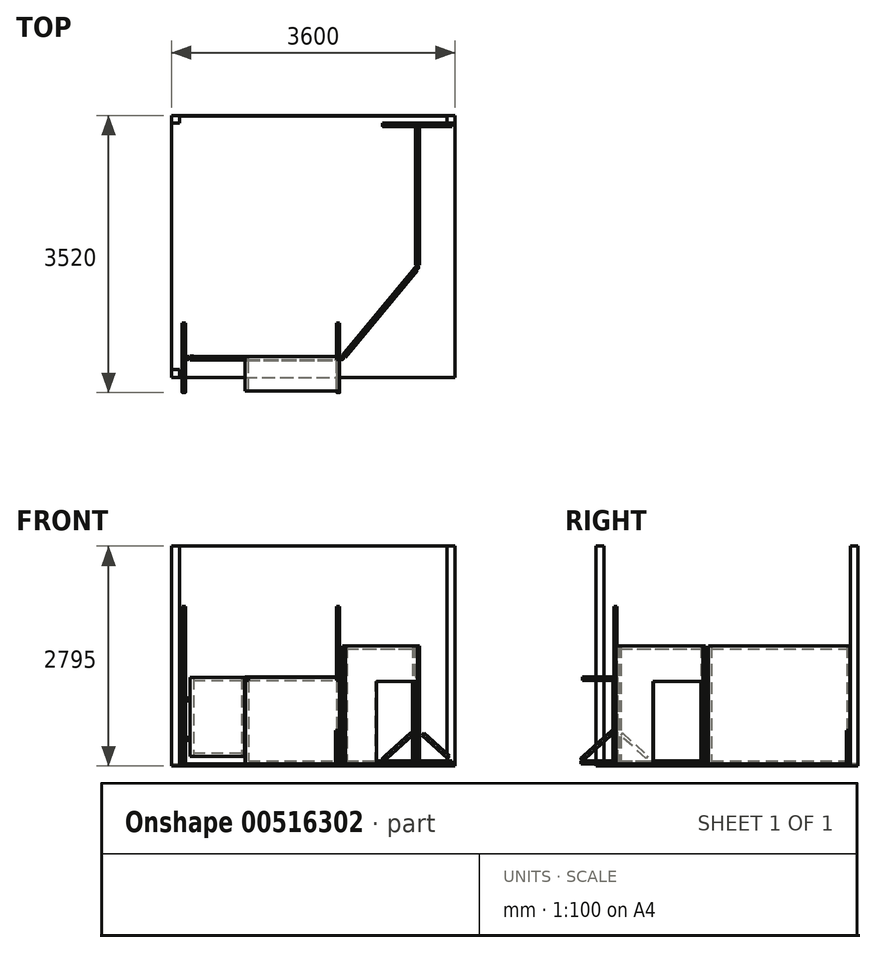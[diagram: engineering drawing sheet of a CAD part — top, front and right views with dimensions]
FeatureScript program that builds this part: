
annotation { "Feature Type Name" : "Feature", "Feature Type Description" : "" }
export const myFeature = defineFeature(function(context is Context, id is Id, definition is map)
    precondition{}
    {
        {
            var Q0;
            Q0=qCreatedBy(makeId("Top.planeOp"),FACE);
            var sketch = newSketch(context, id + "F0", { "sketchPlane" : qUnion([Q0])});
            skLineSegment(sketch, "E0.bottom", {"start": v(-1797.14, 1651.1) * mm, "end": v(1802.86, 1651.1) * mm});
            skLineSegment(sketch, "E0.top", {"start": v(-1797.14, -1678.9) * mm, "end": v(1802.86, -1678.9) * mm});
            skLineSegment(sketch, "E0.left", {"start": v(-1797.14, 1651.1) * mm, "end": v(-1797.14, -1678.9) * mm});
            skLineSegment(sketch, "E0.right", {"start": v(1802.86, 1651.1) * mm, "end": v(1802.86, -1678.9) * mm});
            skSolve(sketch);
        }
        {
            var Q0;
            Q0=makeQuery(id+"F0.imprint","IMPRINT",FACE,{"disambiguationData":[TD([[makeQuery(id+"F0.imprint","IMPRINT",EDGE,{"derivedFrom":sQuery(id+"F0.wireOp",EDGE,"E0.bottom")}),-1.0]])]});
            extrude(context, id + "F1", {"entities" : qUnion([Q0]), "depth" : 25 * mm, "offsetDistance" : 25 * mm});
        }
        {
            var Q0;
            Q0=makeQuery(id+"F1.opExtrude","CAP_FACE",FACE,{"disambiguationData":[OSD([sQuery(id+"F0.wireOp",EDGE,"E0.bottom"),sQuery(id+"F0.wireOp",EDGE,"E0.top"),sQuery(id+"F0.wireOp",EDGE,"E0.left"),sQuery(id+"F0.wireOp",EDGE,"E0.right")])],"isStart":false});
            var sketch = newSketch(context, id + "F2", { "sketchPlane" : qUnion([Q0])});
            skLineSegment(sketch, "E1.bottom", {"start": v(-1797.14, 1651.1) * mm, "end": v(-1697.14, 1651.1) * mm});
            skLineSegment(sketch, "E1.top", {"start": v(-1797.14, 1551.1) * mm, "end": v(-1697.14, 1551.1) * mm});
            skLineSegment(sketch, "E1.left", {"start": v(-1797.14, 1651.1) * mm, "end": v(-1797.14, 1551.1) * mm});
            skLineSegment(sketch, "E1.right", {"start": v(-1697.14, 1651.1) * mm, "end": v(-1697.14, 1551.1) * mm});
            skLineSegment(sketch, "E2.bottom", {"start": v(-1797.14, -1678.9) * mm, "end": v(-1697.14, -1678.9) * mm});
            skLineSegment(sketch, "E2.top", {"start": v(-1797.14, -1578.9) * mm, "end": v(-1697.14, -1578.9) * mm});
            skLineSegment(sketch, "E2.left", {"start": v(-1797.14, -1678.9) * mm, "end": v(-1797.14, -1578.9) * mm});
            skLineSegment(sketch, "E2.right", {"start": v(-1697.14, -1678.9) * mm, "end": v(-1697.14, -1578.9) * mm});
            skLineSegment(sketch, "E3.bottom", {"start": v(1802.86, 1651.1) * mm, "end": v(1702.86, 1651.1) * mm});
            skLineSegment(sketch, "E3.top", {"start": v(1802.86, 1551.1) * mm, "end": v(1702.86, 1551.1) * mm});
            skLineSegment(sketch, "E3.left", {"start": v(1802.86, 1651.1) * mm, "end": v(1802.86, 1551.1) * mm});
            skLineSegment(sketch, "E3.right", {"start": v(1702.86, 1651.1) * mm, "end": v(1702.86, 1551.1) * mm});
            skLineSegment(sketch, "E4.bottom", {"start": v(-1697.14, 1651.1) * mm, "end": v(1702.86, 1651.1) * mm});
            skLineSegment(sketch, "E4.top", {"start": v(-1697.14, 1641.1) * mm, "end": v(1702.86, 1641.1) * mm});
            skLineSegment(sketch, "E4.left", {"start": v(-1697.14, 1651.1) * mm, "end": v(-1697.14, 1641.1) * mm});
            skLineSegment(sketch, "E4.right", {"start": v(1702.86, 1651.1) * mm, "end": v(1702.86, 1641.1) * mm});
            skLineSegment(sketch, "E5.bottom", {"start": v(-1797.14, 1551.1) * mm, "end": v(-1787.14, 1551.1) * mm});
            skLineSegment(sketch, "E5.top", {"start": v(-1797.14, -1578.9) * mm, "end": v(-1787.14, -1578.9) * mm});
            skLineSegment(sketch, "E5.left", {"start": v(-1797.14, 1551.1) * mm, "end": v(-1797.14, -1578.9) * mm});
            skLineSegment(sketch, "E5.right", {"start": v(-1787.14, 1551.1) * mm, "end": v(-1787.14, -1578.9) * mm});
            skSolve(sketch);
        }
        {
            var Q0;
            Q0=makeQuery(id+"F2.imprint","IMPRINT",FACE,{"disambiguationData":[TD([[makeQuery(id+"F2.imprint","IMPRINT",EDGE,{"derivedFrom":sQuery(id+"F2.wireOp",EDGE,"E1.bottom")}),-1.0]])]});
            var Q1;
            Q1=makeQuery(id+"F2.imprint","IMPRINT",FACE,{"disambiguationData":[TD([[makeQuery(id+"F2.imprint","IMPRINT",EDGE,{"derivedFrom":sQuery(id+"F2.wireOp",EDGE,"E2.bottom")}),1.0]])]});
            var Q2;
            Q2=makeQuery(id+"F2.imprint","IMPRINT",FACE,{"disambiguationData":[TD([[makeQuery(id+"F2.imprint","IMPRINT",EDGE,{"derivedFrom":sQuery(id+"F2.wireOp",EDGE,"rSnRhUeP-VmXx-mMHw-5nAW-2HBpdxi9ySfm.bottom")}),1.0]])]});
            var Q3;
            Q3=makeQuery(id+"F2.imprint","IMPRINT",FACE,{"disambiguationData":[TD([[makeQuery(id+"F2.imprint","IMPRINT",EDGE,{"derivedFrom":sQuery(id+"F2.wireOp",EDGE,"E3.bottom")}),-1.0]])]});
            var Q4;
            Q4=makeQuery(id+"F2.imprint","IMPRINT",FACE,{"disambiguationData":[TD([[makeQuery(id+"F2.imprint","IMPRINT",EDGE,{"derivedFrom":sQuery(id+"F2.wireOp",EDGE,"E5.bottom")}),-1.0]])]});
            var Q5;
            Q5=makeQuery(id+"F2.imprint","IMPRINT",FACE,{"disambiguationData":[TD([[makeQuery(id+"F2.imprint","IMPRINT",EDGE,{"derivedFrom":sQuery(id+"F2.wireOp",EDGE,"E4.bottom")}),-1.0]])]});
            extrude(context, id + "F3", {"entities" : qUnion([Q0, Q1, Q2, Q3, Q4, Q5]), "operationType" : NewBodyOperationType.ADD, "depth" : 2770 * mm, "offsetDistance" : 25 * mm});
        }
        {
            var Q0;
            Q0=makeQuery(id+"F1.opExtrude","CAP_FACE",FACE,{"disambiguationData":[OSD([sQuery(id+"F0.wireOp",EDGE,"E0.bottom"),sQuery(id+"F0.wireOp",EDGE,"E0.top"),sQuery(id+"F0.wireOp",EDGE,"E0.left"),sQuery(id+"F0.wireOp",EDGE,"E0.right")])],"isStart":false});
            var sketch = newSketch(context, id + "F4", { "sketchPlane" : qUnion([Q0])});
            skLineSegment(sketch, "E6.bottom", {"start": v(1302.86, 1551.1) * mm, "end": v(1342.86, 1551.1) * mm});
            skLineSegment(sketch, "E6.top", {"start": v(1302.86, 1511.1) * mm, "end": v(1342.86, 1511.1) * mm});
            skLineSegment(sketch, "E6.left", {"start": v(1302.86, 1551.1) * mm, "end": v(1302.86, 1511.1) * mm});
            skLineSegment(sketch, "E6.right", {"start": v(1342.86, 1551.1) * mm, "end": v(1342.86, 1511.1) * mm});
            skLineSegment(sketch, "E7.bottom", {"start": v(1302.86, -208.9) * mm, "end": v(1342.86, -208.9) * mm});
            skLineSegment(sketch, "E7.top", {"start": v(1302.86, -248.9) * mm, "end": v(1342.86, -248.9) * mm});
            skLineSegment(sketch, "E7.left", {"start": v(1302.86, -208.9) * mm, "end": v(1302.86, -248.9) * mm});
            skLineSegment(sketch, "E7.right", {"start": v(1342.86, -208.9) * mm, "end": v(1342.86, -248.9) * mm});
            skLineSegment(sketch, "E8.bottom", {"start": v(-1660.5, -1408.9) * mm, "end": v(-1620.5, -1408.9) * mm});
            skLineSegment(sketch, "E8.top", {"start": v(-1660.5, -1448.9) * mm, "end": v(-1620.5, -1448.9) * mm});
            skLineSegment(sketch, "E8.left", {"start": v(-1660.5, -1408.9) * mm, "end": v(-1660.5, -1448.9) * mm});
            skLineSegment(sketch, "E8.right", {"start": v(-1620.5, -1408.9) * mm, "end": v(-1620.5, -1448.9) * mm});
            skLineSegment(sketch, "E9.bottom", {"start": v(299.5, -1408.9) * mm, "end": v(339.5, -1408.9) * mm});
            skLineSegment(sketch, "E9.top", {"start": v(299.5, -1448.9) * mm, "end": v(339.5, -1448.9) * mm});
            skLineSegment(sketch, "E9.left", {"start": v(299.5, -1408.9) * mm, "end": v(299.5, -1448.9) * mm});
            skLineSegment(sketch, "E9.right", {"start": v(339.5, -1408.9) * mm, "end": v(339.5, -1448.9) * mm});
            skSolve(sketch);
        }
        {
            var Q0;
            Q0=makeQuery(id+"F4.imprint","IMPRINT",FACE,{"disambiguationData":[TD([[makeQuery(id+"F4.imprint","IMPRINT",EDGE,{"derivedFrom":sQuery(id+"F4.wireOp",EDGE,"E6.bottom")}),-1.0]])]});
            var Q1;
            Q1=makeQuery(id+"F4.imprint","IMPRINT",FACE,{"disambiguationData":[TD([[makeQuery(id+"F4.imprint","IMPRINT",EDGE,{"derivedFrom":sQuery(id+"F4.wireOp",EDGE,"E7.bottom")}),-1.0]])]});
            extrude(context, id + "F5", {"entities" : qUnion([Q0, Q1]), "operationType" : NewBodyOperationType.ADD, "depth" : 1500 * mm, "offsetDistance" : 25 * mm});
        }
        {
            var Q0;
            Q0=makeQuery(id+"F4.imprint","IMPRINT",FACE,{"disambiguationData":[TD([[makeQuery(id+"F4.imprint","IMPRINT",EDGE,{"derivedFrom":sQuery(id+"F4.wireOp",EDGE,"E8.bottom")}),-1.0]])]});
            var Q1;
            Q1=makeQuery(id+"F4.imprint","IMPRINT",FACE,{"disambiguationData":[TD([[makeQuery(id+"F4.imprint","IMPRINT",EDGE,{"derivedFrom":sQuery(id+"F4.wireOp",EDGE,"E9.bottom")}),-1.0]])]});
            extrude(context, id + "F6", {"entities" : qUnion([Q0, Q1]), "operationType" : NewBodyOperationType.ADD, "depth" : 2000 * mm, "offsetDistance" : 25 * mm});
        }
        {
            var Q0;
            Q0=makeQuery(id+"F5.opExtrude","SWEPT_FACE",FACE,{"disambiguationData":[OSD([sQuery(id+"F4.wireOp",EDGE,"E6.top")])]});
            var sketch = newSketch(context, id + "F7", { "sketchPlane" : qUnion([Q0])});
            skLineSegment(sketch, "E10.bottom", {"start": v(1302.86, 1525) * mm, "end": v(1342.86, 1525) * mm});
            skLineSegment(sketch, "E10.top", {"start": v(1302.86, 1485) * mm, "end": v(1342.86, 1485) * mm});
            skLineSegment(sketch, "E10.left", {"start": v(1302.86, 1525) * mm, "end": v(1302.86, 1485) * mm});
            skLineSegment(sketch, "E10.right", {"start": v(1342.86, 1525) * mm, "end": v(1342.86, 1485) * mm});
            skLineSegment(sketch, "E11.bottom", {"start": v(1302.86, 25) * mm, "end": v(1342.86, 25) * mm});
            skLineSegment(sketch, "E11.top", {"start": v(1302.86, 65) * mm, "end": v(1342.86, 65) * mm});
            skLineSegment(sketch, "E11.left", {"start": v(1302.86, 25) * mm, "end": v(1302.86, 65) * mm});
            skLineSegment(sketch, "E11.right", {"start": v(1342.86, 25) * mm, "end": v(1342.86, 65) * mm});
            skSolve(sketch);
        }
        {
            var Q0;
            Q0=makeQuery(id+"F7.imprint","IMPRINT",FACE,{"disambiguationData":[TD([[makeQuery(id+"F7.imprint","IMPRINT",EDGE,{"derivedFrom":sQuery(id+"F7.wireOp",EDGE,"E10.bottom")}),-1.0]])]});
            var Q1;
            Q1=makeQuery(id+"F7.imprint","IMPRINT",FACE,{"disambiguationData":[TD([[makeQuery(id+"F7.imprint","IMPRINT",EDGE,{"derivedFrom":sQuery(id+"F7.wireOp",EDGE,"E11.bottom")}),1.0]])]});
            extrude(context, id + "F8", {"entities" : qUnion([Q0, Q1]), "depth" : 1720 * mm, "offsetDistance" : 25 * mm});
        }
        {
            var Q0;
            Q0=makeQuery(id+"F5.opExtrude","SWEPT_FACE",FACE,{"disambiguationData":[OSD([sQuery(id+"F4.wireOp",EDGE,"E6.top")])]});
            var sketch = newSketch(context, id + "F9", { "sketchPlane" : qUnion([Q0])});
            skCircle(sketch, "E12", {"center": v(1272.86, 425) * mm, "radius": 20 * mm});
            skCircle(sketch, "E13", {"center": v(902.86, 95) * mm, "radius": 20 * mm});
            skLineSegment(sketch, "E14", {"start": v(1259.54, 439.93) * mm, "end": v(1259.54, 439.93) * mm});
            skLineSegment(sketch, "E15", {"start": v(938.56, 100.04) * mm, "end": v(1263.78, 390.1) * mm});
            skLineSegment(sketch, "E16", {"start": v(911.93, 129.9) * mm, "end": v(938.56, 100.04) * mm});
            skLineSegment(sketch, "E17", {"start": v(1237.15, 419.96) * mm, "end": v(1263.78, 390.1) * mm});
            skLineSegment(sketch, "E18.trimOffspring", {"start": v(1237.15, 419.96) * mm, "end": v(911.93, 129.9) * mm});
            skLineSegment(sketch, "E19.bottom", {"start": v(1302.86, 65) * mm, "end": v(882.86, 65) * mm});
            skLineSegment(sketch, "E19.top", {"start": v(1302.86, 25) * mm, "end": v(882.86, 25) * mm});
            skLineSegment(sketch, "E19.left", {"start": v(1302.86, 65) * mm, "end": v(1302.86, 25) * mm});
            skLineSegment(sketch, "E19.right", {"start": v(882.86, 65) * mm, "end": v(882.86, 25) * mm});
            skLineSegment(sketch, "E20", {"start": v(1322.86, 66.16) * mm, "end": v(1322.86, 454.53) * mm, "construction": true});
            skCircle(sketch, "E21.MirrorC", {"center": v(1372.86, 425) * mm, "radius": 20 * mm});
            skLineSegment(sketch, "E22.MirrorCS", {"start": v(1408.56, 419.96) * mm, "end": v(1381.93, 390.1) * mm});
            skLineSegment(sketch, "E23.MirrorCS", {"start": v(1408.56, 419.96) * mm, "end": v(1733.78, 129.9) * mm});
            skLineSegment(sketch, "E24.MirrorCS", {"start": v(1707.15, 100.04) * mm, "end": v(1381.93, 390.1) * mm});
            skLineSegment(sketch, "E25.MirrorCS", {"start": v(1733.78, 129.9) * mm, "end": v(1707.15, 100.04) * mm});
            skCircle(sketch, "E26.MirrorC", {"center": v(1742.86, 95) * mm, "radius": 20 * mm});
            skLineSegment(sketch, "E27.MirrorCS", {"start": v(1762.86, 65) * mm, "end": v(1762.86, 25) * mm});
            skLineSegment(sketch, "E28.MirrorCS", {"start": v(1342.86, 65) * mm, "end": v(1762.86, 65) * mm});
            skLineSegment(sketch, "E29.MirrorCS", {"start": v(1342.86, 25) * mm, "end": v(1762.86, 25) * mm});
            skLineSegment(sketch, "E30.MirrorCS", {"start": v(1342.86, 65) * mm, "end": v(1342.86, 25) * mm});
            skSolve(sketch);
        }
        {
            var Q0;
            Q0=makeQuery(id+"F9.imprint","IMPRINT",FACE,{"disambiguationData":[TD([[makeQuery(id+"F9.imprint","IMPRINT",EDGE,{"derivedFrom":sQuery(id+"F9.wireOp",EDGE,"E15")}),1.0]])]});
            var Q1;
            Q1=makeQuery(id+"F9.imprint","IMPRINT",FACE,{"disambiguationData":[TD([[makeQuery(id+"F9.imprint","IMPRINT",EDGE,{"derivedFrom":sQuery(id+"F9.wireOp",EDGE,"E12")}),1.0]])]});
            var Q2;
            Q2=makeQuery(id+"F9.imprint","IMPRINT",FACE,{"disambiguationData":[TD([[makeQuery(id+"F9.imprint","IMPRINT",EDGE,{"derivedFrom":sQuery(id+"F9.wireOp",EDGE,"E13")}),1.0]])]});
            var Q3;
            Q3=makeQuery(id+"F9.imprint","IMPRINT",FACE,{"disambiguationData":[TD([[makeQuery(id+"F9.imprint","IMPRINT",EDGE,{"derivedFrom":sQuery(id+"F9.wireOp",EDGE,"E19.bottom")}),1.0]])]});
            var Q4;
            Q4=makeQuery(id+"F9.imprint","IMPRINT",FACE,{"disambiguationData":[TD([[makeQuery(id+"F9.imprint","IMPRINT",EDGE,{"derivedFrom":sQuery(id+"F9.wireOp",EDGE,"E21.MirrorC")}),-1.0]])]});
            var Q5;
            Q5=makeQuery(id+"F9.imprint","IMPRINT",FACE,{"disambiguationData":[TD([[makeQuery(id+"F9.imprint","IMPRINT",EDGE,{"derivedFrom":sQuery(id+"F9.wireOp",EDGE,"E22.MirrorCS")}),1.0]])]});
            var Q6;
            Q6=makeQuery(id+"F9.imprint","IMPRINT",FACE,{"disambiguationData":[TD([[makeQuery(id+"F9.imprint","IMPRINT",EDGE,{"derivedFrom":sQuery(id+"F9.wireOp",EDGE,"E26.MirrorC")}),-1.0]])]});
            var Q7;
            Q7=makeQuery(id+"F9.imprint","IMPRINT",FACE,{"disambiguationData":[TD([[makeQuery(id+"F9.imprint","IMPRINT",EDGE,{"derivedFrom":sQuery(id+"F9.wireOp",EDGE,"E27.MirrorCS")}),-1.0]])]});
            extrude(context, id + "F10", {"entities" : qUnion([Q0, Q1, Q2, Q3, Q4, Q5, Q6, Q7]), "oppositeDirection" : true, "depth" : 40 * mm, "offsetDistance" : 25 * mm});
        }
        {
            var Q0;
            Q0=makeQuery(id+"F6.opExtrude","SWEPT_FACE",FACE,{"disambiguationData":[OSD([sQuery(id+"F4.wireOp",EDGE,"E8.right")])]});
            var sketch = newSketch(context, id + "F11", { "sketchPlane" : qUnion([Q0])});
            skCircle(sketch, "E31", {"center": v(-1478.9, 425) * mm, "radius": 20 * mm});
            skCircle(sketch, "E32", {"center": v(-1848.9, 95) * mm, "radius": 20 * mm});
            skLineSegment(sketch, "E33", {"start": v(-1492.2, 439.93) * mm, "end": v(-1492.2, 439.93) * mm});
            skLineSegment(sketch, "E34", {"start": v(-1813.19, 100.04) * mm, "end": v(-1487.97, 390.1) * mm});
            skLineSegment(sketch, "E35", {"start": v(-1839.81, 129.9) * mm, "end": v(-1813.19, 100.04) * mm});
            skLineSegment(sketch, "E36", {"start": v(-1514.6, 419.96) * mm, "end": v(-1487.97, 390.1) * mm});
            skLineSegment(sketch, "E37.trimOffspring", {"start": v(-1514.6, 419.96) * mm, "end": v(-1839.81, 129.9) * mm});
            skLineSegment(sketch, "E38.bottom", {"start": v(-1448.9, 65) * mm, "end": v(-1868.9, 65) * mm});
            skLineSegment(sketch, "E38.top", {"start": v(-1448.9, 25) * mm, "end": v(-1868.9, 25) * mm});
            skLineSegment(sketch, "E38.left", {"start": v(-1448.9, 65) * mm, "end": v(-1448.9, 25) * mm});
            skLineSegment(sketch, "E38.right", {"start": v(-1868.9, 65) * mm, "end": v(-1868.9, 25) * mm});
            skLineSegment(sketch, "E39", {"start": v(-1428.9, 66.16) * mm, "end": v(-1428.9, 454.53) * mm, "construction": true});
            skCircle(sketch, "E40.MirrorC", {"center": v(-1378.9, 425) * mm, "radius": 20 * mm});
            skLineSegment(sketch, "E41.MirrorCS", {"start": v(-1343.19, 419.96) * mm, "end": v(-1369.81, 390.1) * mm});
            skLineSegment(sketch, "E42.MirrorCS", {"start": v(-1343.19, 419.96) * mm, "end": v(-1017.97, 129.9) * mm});
            skLineSegment(sketch, "E43.MirrorCS", {"start": v(-1044.6, 100.04) * mm, "end": v(-1369.81, 390.1) * mm});
            skLineSegment(sketch, "E44.MirrorCS", {"start": v(-1017.97, 129.9) * mm, "end": v(-1044.6, 100.04) * mm});
            skCircle(sketch, "E45.MirrorC", {"center": v(-1008.9, 95) * mm, "radius": 20 * mm});
            skLineSegment(sketch, "E46.MirrorCS", {"start": v(-988.9, 65) * mm, "end": v(-988.9, 25) * mm});
            skLineSegment(sketch, "E47.MirrorCS", {"start": v(-1408.9, 65) * mm, "end": v(-988.9, 65) * mm});
            skLineSegment(sketch, "E48.MirrorCS", {"start": v(-1408.9, 25) * mm, "end": v(-988.9, 25) * mm});
            skLineSegment(sketch, "E49.MirrorCS", {"start": v(-1408.9, 65) * mm, "end": v(-1408.9, 25) * mm});
            skSolve(sketch);
        }
        {
            var Q0;
            Q0=makeQuery(id+"F11.imprint","IMPRINT",FACE,{"disambiguationData":[TD([[makeQuery(id+"F11.imprint","IMPRINT",EDGE,{"derivedFrom":sQuery(id+"F11.wireOp",EDGE,"E34")}),1.0]])]});
            var Q1;
            Q1=makeQuery(id+"F11.imprint","IMPRINT",FACE,{"disambiguationData":[TD([[makeQuery(id+"F11.imprint","IMPRINT",EDGE,{"derivedFrom":sQuery(id+"F11.wireOp",EDGE,"E31")}),1.0]])]});
            var Q2;
            Q2=makeQuery(id+"F11.imprint","IMPRINT",FACE,{"disambiguationData":[TD([[makeQuery(id+"F11.imprint","IMPRINT",EDGE,{"derivedFrom":sQuery(id+"F11.wireOp",EDGE,"E32")}),1.0]])]});
            var Q3;
            {var subQ0=sQuery(id+"F11.wireOp",EDGE,"E38.right");Q3=makeQuery(id+"F11.imprint","IMPRINT",FACE,{"disambiguationData":[TD([[makeQuery(id+"F11.imprint","IMPRINT",EDGE,{"derivedFrom":subQ0}),1.0]])]});}
            var Q4;
            Q4=makeQuery(id+"F11.imprint","IMPRINT",FACE,{"disambiguationData":[TD([[makeQuery(id+"F11.imprint","IMPRINT",EDGE,{"derivedFrom":sQuery(id+"F11.wireOp",EDGE,"E46.MirrorCS")}),-1.0]])]});
            var Q5;
            Q5=makeQuery(id+"F11.imprint","IMPRINT",FACE,{"disambiguationData":[TD([[makeQuery(id+"F11.imprint","IMPRINT",EDGE,{"derivedFrom":sQuery(id+"F11.wireOp",EDGE,"E45.MirrorC")}),-1.0]])]});
            var Q6;
            Q6=makeQuery(id+"F11.imprint","IMPRINT",FACE,{"disambiguationData":[TD([[makeQuery(id+"F11.imprint","IMPRINT",EDGE,{"derivedFrom":sQuery(id+"F11.wireOp",EDGE,"E41.MirrorCS")}),1.0]])]});
            var Q7;
            Q7=makeQuery(id+"F11.imprint","IMPRINT",FACE,{"disambiguationData":[TD([[makeQuery(id+"F11.imprint","IMPRINT",EDGE,{"derivedFrom":sQuery(id+"F11.wireOp",EDGE,"E40.MirrorC")}),-1.0]])]});
            extrude(context, id + "F12", {"entities" : qUnion([Q0, Q1, Q2, Q3, Q4, Q5, Q6, Q7]), "operationType" : NewBodyOperationType.ADD, "oppositeDirection" : true, "depth" : 40 * mm, "offsetDistance" : 25 * mm});
        }
        {
            var Q0;
            Q0=makeQuery(id+"F6.opExtrude","SWEPT_FACE",FACE,{"disambiguationData":[OSD([sQuery(id+"F4.wireOp",EDGE,"E9.right")])]});
            var sketch = newSketch(context, id + "F13", { "sketchPlane" : qUnion([Q0])});
            skCircle(sketch, "E50", {"center": v(-1478.9, 425) * mm, "radius": 20 * mm});
            skCircle(sketch, "E51", {"center": v(-1848.9, 95) * mm, "radius": 20 * mm});
            skLineSegment(sketch, "E52", {"start": v(-1492.2, 439.93) * mm, "end": v(-1492.2, 439.93) * mm});
            skLineSegment(sketch, "E53", {"start": v(-1813.19, 100.04) * mm, "end": v(-1487.97, 390.1) * mm});
            skLineSegment(sketch, "E54", {"start": v(-1839.81, 129.9) * mm, "end": v(-1813.19, 100.04) * mm});
            skLineSegment(sketch, "E55", {"start": v(-1514.6, 419.96) * mm, "end": v(-1487.97, 390.1) * mm});
            skLineSegment(sketch, "E56.trimOffspring", {"start": v(-1514.6, 419.96) * mm, "end": v(-1839.81, 129.9) * mm});
            skLineSegment(sketch, "E57.bottom", {"start": v(-1448.9, 65) * mm, "end": v(-1868.9, 65) * mm});
            skLineSegment(sketch, "E57.top", {"start": v(-1448.9, 25) * mm, "end": v(-1868.9, 25) * mm});
            skLineSegment(sketch, "E57.left", {"start": v(-1448.9, 65) * mm, "end": v(-1448.9, 25) * mm});
            skLineSegment(sketch, "E57.right", {"start": v(-1868.9, 65) * mm, "end": v(-1868.9, 25) * mm});
            skLineSegment(sketch, "E58", {"start": v(-1428.9, 66.16) * mm, "end": v(-1428.9, 454.53) * mm, "construction": true});
            skCircle(sketch, "E59.MirrorC", {"center": v(-1378.9, 425) * mm, "radius": 20 * mm});
            skLineSegment(sketch, "E60.MirrorCS", {"start": v(-1343.19, 419.96) * mm, "end": v(-1369.81, 390.1) * mm});
            skLineSegment(sketch, "E61.MirrorCS", {"start": v(-1343.19, 419.96) * mm, "end": v(-1017.97, 129.9) * mm});
            skLineSegment(sketch, "E62.MirrorCS", {"start": v(-1044.6, 100.04) * mm, "end": v(-1369.81, 390.1) * mm});
            skLineSegment(sketch, "E63.MirrorCS", {"start": v(-1017.97, 129.9) * mm, "end": v(-1044.6, 100.04) * mm});
            skCircle(sketch, "E64.MirrorC", {"center": v(-1008.9, 95) * mm, "radius": 20 * mm});
            skLineSegment(sketch, "E65.MirrorCS", {"start": v(-988.9, 65) * mm, "end": v(-988.9, 25) * mm});
            skLineSegment(sketch, "E66.MirrorCS", {"start": v(-1408.9, 65) * mm, "end": v(-988.9, 65) * mm});
            skLineSegment(sketch, "E67.MirrorCS", {"start": v(-1408.9, 25) * mm, "end": v(-988.9, 25) * mm});
            skLineSegment(sketch, "E68.MirrorCS", {"start": v(-1408.9, 65) * mm, "end": v(-1408.9, 25) * mm});
            skSolve(sketch);
        }
        {
            var Q0;
            {var subQ0=sQuery(id+"F13.wireOp",EDGE,"E57.right");Q0=makeQuery(id+"F13.imprint","IMPRINT",FACE,{"disambiguationData":[TD([[makeQuery(id+"F13.imprint","IMPRINT",EDGE,{"derivedFrom":subQ0}),1.0]])]});}
            var Q1;
            Q1=makeQuery(id+"F13.imprint","IMPRINT",FACE,{"disambiguationData":[TD([[makeQuery(id+"F13.imprint","IMPRINT",EDGE,{"derivedFrom":sQuery(id+"F13.wireOp",EDGE,"E51")}),1.0]])]});
            var Q2;
            Q2=makeQuery(id+"F13.imprint","IMPRINT",FACE,{"disambiguationData":[TD([[makeQuery(id+"F13.imprint","IMPRINT",EDGE,{"derivedFrom":sQuery(id+"F13.wireOp",EDGE,"E53")}),1.0]])]});
            var Q3;
            Q3=makeQuery(id+"F13.imprint","IMPRINT",FACE,{"disambiguationData":[TD([[makeQuery(id+"F13.imprint","IMPRINT",EDGE,{"derivedFrom":sQuery(id+"F13.wireOp",EDGE,"E50")}),1.0]])]});
            var Q4;
            Q4=makeQuery(id+"F13.imprint","IMPRINT",FACE,{"disambiguationData":[TD([[makeQuery(id+"F13.imprint","IMPRINT",EDGE,{"derivedFrom":sQuery(id+"F13.wireOp",EDGE,"E59.MirrorC")}),-1.0]])]});
            var Q5;
            Q5=makeQuery(id+"F13.imprint","IMPRINT",FACE,{"disambiguationData":[TD([[makeQuery(id+"F13.imprint","IMPRINT",EDGE,{"derivedFrom":sQuery(id+"F13.wireOp",EDGE,"E60.MirrorCS")}),1.0]])]});
            var Q6;
            Q6=makeQuery(id+"F13.imprint","IMPRINT",FACE,{"disambiguationData":[TD([[makeQuery(id+"F13.imprint","IMPRINT",EDGE,{"derivedFrom":sQuery(id+"F13.wireOp",EDGE,"E64.MirrorC")}),-1.0]])]});
            var Q7;
            Q7=makeQuery(id+"F13.imprint","IMPRINT",FACE,{"disambiguationData":[TD([[makeQuery(id+"F13.imprint","IMPRINT",EDGE,{"derivedFrom":sQuery(id+"F13.wireOp",EDGE,"E65.MirrorCS")}),-1.0]])]});
            extrude(context, id + "F14", {"entities" : qUnion([Q0, Q1, Q2, Q3, Q4, Q5, Q6, Q7]), "operationType" : NewBodyOperationType.ADD, "oppositeDirection" : true, "depth" : 40 * mm, "offsetDistance" : 25 * mm});
        }
        {
            var Q0;
            Q0=makeQuery(id+"F12.boolean.opBoolean","MERGE",FACE,{"derivedFrom":[makeQuery(id+"F6.opExtrude","SWEPT_FACE",FACE,{"disambiguationData":[OSD([sQuery(id+"F4.wireOp",EDGE,"E8.right")])]}),makeQuery(id+"F12.opExtrude","CAP_FACE",FACE,{"disambiguationData":[OSD([sQuery(id+"F11.wireOp",EDGE,"E38.bottom"),sQuery(id+"F11.wireOp",EDGE,"E38.top"),sQuery(id+"F11.wireOp",EDGE,"E38.left"),sQuery(id+"F11.wireOp",EDGE,"E38.right")])],"isStart":true}),makeQuery(id+"F12.opExtrude","CAP_FACE",FACE,{"disambiguationData":[OSD([sQuery(id+"F11.wireOp",EDGE,"E46.MirrorCS"),sQuery(id+"F11.wireOp",EDGE,"E47.MirrorCS"),sQuery(id+"F11.wireOp",EDGE,"E48.MirrorCS"),sQuery(id+"F11.wireOp",EDGE,"E49.MirrorCS")])],"isStart":true})]});
            var sketch = newSketch(context, id + "F15", { "sketchPlane" : qUnion([Q0])});
            skLineSegment(sketch, "E69.bottom", {"start": v(-1448.9, 1085) * mm, "end": v(-1408.9, 1085) * mm});
            skLineSegment(sketch, "E69.top", {"start": v(-1448.9, 1125) * mm, "end": v(-1408.9, 1125) * mm});
            skLineSegment(sketch, "E69.left", {"start": v(-1448.9, 1085) * mm, "end": v(-1448.9, 1125) * mm});
            skLineSegment(sketch, "E69.right", {"start": v(-1408.9, 1085) * mm, "end": v(-1408.9, 1125) * mm});
            skLineSegment(sketch, "E70.bottom", {"start": v(-1408.9, 65) * mm, "end": v(-1448.9, 65) * mm});
            skLineSegment(sketch, "E70.top", {"start": v(-1408.9, 25) * mm, "end": v(-1448.9, 25) * mm});
            skLineSegment(sketch, "E70.left", {"start": v(-1408.9, 65) * mm, "end": v(-1408.9, 25) * mm});
            skLineSegment(sketch, "E70.right", {"start": v(-1448.9, 65) * mm, "end": v(-1448.9, 25) * mm});
            skSolve(sketch);
        }
        {
            var Q0;
            Q0=makeQuery(id+"FTKCVcSfVxfKRfc_25.boolean.opBoolean","MERGE",FACE,{"derivedFrom":[makeQuery(id+"F6.opExtrude","SWEPT_FACE",FACE,{"disambiguationData":[OSD([sQuery(id+"F4.wireOp",EDGE,"E8.top")])]}),makeQuery(id+"F6.opExtrude","SWEPT_FACE",FACE,{"disambiguationData":[OSD([sQuery(id+"F4.wireOp",EDGE,"E9.top")])]}),makeQuery(id+"FTKCVcSfVxfKRfc_25.opExtrude","SWEPT_FACE",FACE,{"disambiguationData":[OSD([sQuery(id+"F15.wireOp",EDGE,"E69.left")])]})]});
            var sketch = newSketch(context, id + "F16", { "sketchPlane" : qUnion([Q0])});
            skLineSegment(sketch, "E71.bottom", {"start": v(299.5, 1125) * mm, "end": v(339.5, 1125) * mm});
            skLineSegment(sketch, "E71.top", {"start": v(299.5, 1085) * mm, "end": v(339.5, 1085) * mm});
            skLineSegment(sketch, "E71.left", {"start": v(299.5, 1125) * mm, "end": v(299.5, 1085) * mm});
            skLineSegment(sketch, "E71.right", {"start": v(339.5, 1125) * mm, "end": v(339.5, 1085) * mm});
            skSolve(sketch);
        }
        {
            var Q0;
            Q0=makeQuery(id+"F16.imprint","IMPRINT",FACE,{"disambiguationData":[TD([[makeQuery(id+"F16.imprint","IMPRINT",EDGE,{"derivedFrom":sQuery(id+"F16.wireOp",EDGE,"qD92tVp6-3oIY-8GjO-ZRrK-SN2lZ3PL9uU9.bottom")}),1.0]])]});
            var Q1;
            Q1=makeQuery(id+"F16.imprint","IMPRINT",FACE,{"disambiguationData":[TD([[makeQuery(id+"F16.imprint","IMPRINT",EDGE,{"derivedFrom":sQuery(id+"F16.wireOp",EDGE,"E71.bottom")}),-1.0]])]});
            extrude(context, id + "F17", {"entities" : qUnion([Q0, Q1]), "operationType" : NewBodyOperationType.ADD, "depth" : 400 * mm, "offsetDistance" : 25 * mm});
        }
        {
            var Q0;
            Q0=makeQuery(id+"F4.imprint","IMPRINT",FACE,{"disambiguationData":[TD([[makeQuery(id+"F4.imprint","IMPRINT",EDGE,{"derivedFrom":sQuery(id+"F4.wireOp",EDGE,"E6.bottom")}),1.0]])]});
            cPlane(context, id + "F18", {"entities" : qUnion([Q0]), "cplaneType" : CPlaneType.OFFSET, "offset" : 400 * mm, "width" : 150 * mm, "height" : 150 * mm});
        }
        {
            var Q0;
            Q0=qCreatedBy(id+"F18.planeOp",FACE);
            var sketch = newSketch(context, id + "F19", { "sketchPlane" : qUnion([Q0])});
            skCircle(sketch, "E72", {"center": v(1322.86, -278.9) * mm, "radius": 20 * mm});
            skCircle(sketch, "E73", {"center": v(369.5, -1428.9) * mm, "radius": 20 * mm});
            skSolve(sketch);
        }
        {
            var Q0;
            Q0 = qSketchRegion(id + "F19", true);
            extrude(context, id + "F20", {"entities" : qUnion([Q0]), "depth" : 40 * mm, "offsetDistance" : 25 * mm});
        }
        {
            var Q0;
            Q0=makeQuery(id+"F4.imprint","IMPRINT",FACE,{"disambiguationData":[TD([[makeQuery(id+"F4.imprint","IMPRINT",EDGE,{"derivedFrom":sQuery(id+"F4.wireOp",EDGE,"E6.bottom")}),1.0]])]});
            cPlane(context, id + "F21", {"entities" : qUnion([Q0]), "cplaneType" : CPlaneType.OFFSET, "offset" : 1100 * mm, "width" : 150 * mm, "height" : 150 * mm});
        }
        {
            var Q0;
            Q0=qCreatedBy(id+"F21.planeOp",FACE);
            var sketch = newSketch(context, id + "F22", { "sketchPlane" : qUnion([Q0])});
            skCircle(sketch, "E74", {"center": v(1322.86, -278.9) * mm, "radius": 20 * mm});
            skCircle(sketch, "E75", {"center": v(369.5, -1428.9) * mm, "radius": 20 * mm});
            skSolve(sketch);
        }
        {
            var Q0;
            Q0=makeQuery(id+"F22.imprint","IMPRINT",FACE,{"disambiguationData":[TD([[makeQuery(id+"F22.imprint","IMPRINT",EDGE,{"derivedFrom":sQuery(id+"F22.wireOp",EDGE,"E74")}),1.0]])]});
            var Q1;
            Q1=makeQuery(id+"F22.imprint","IMPRINT",FACE,{"disambiguationData":[TD([[makeQuery(id+"F22.imprint","IMPRINT",EDGE,{"derivedFrom":sQuery(id+"F22.wireOp",EDGE,"E75")}),1.0]])]});
            extrude(context, id + "F23", {"entities" : qUnion([Q0, Q1]), "depth" : 40 * mm, "offsetDistance" : 25 * mm});
        }
        {
            var Q0;
            Q0=makeQuery(id+"F4.imprint","IMPRINT",FACE,{"disambiguationData":[TD([[makeQuery(id+"F4.imprint","IMPRINT",EDGE,{"derivedFrom":sQuery(id+"F4.wireOp",EDGE,"E6.bottom")}),1.0]])]});
            cPlane(context, id + "F24", {"entities" : qUnion([Q0]), "cplaneType" : CPlaneType.OFFSET, "offset" : 0 * mm, "width" : 150 * mm, "height" : 150 * mm});
        }
        {
            var Q0;
            Q0=qCreatedBy(id+"F24.planeOp",FACE);
            var sketch = newSketch(context, id + "F25", { "sketchPlane" : qUnion([Q0])});
            skLineSegment(sketch, "E76", {"start": v(1262.78, -320.02) * mm, "end": v(1288.31, -289.22) * mm});
            skLineSegment(sketch, "E77", {"start": v(1288.31, -289.22) * mm, "end": v(1319.1, -314.75) * mm});
            skLineSegment(sketch, "E78", {"start": v(1319.1, -314.75) * mm, "end": v(1293.58, -345.55) * mm});
            skLineSegment(sketch, "E79", {"start": v(1293.58, -345.55) * mm, "end": v(1262.78, -320.02) * mm});
            skCircle(sketch, "E80", {"center": v(1322.86, -278.9) * mm, "radius": 20 * mm, "construction": true});
            skPoint(sketch, "E81.start.orphan", {"position": v(346.25, -1400.26) * mm});
            skCircle(sketch, "E82", {"center": v(369.5, -1428.9) * mm, "radius": 20 * mm, "construction": true});
            skLineSegment(sketch, "E83", {"start": v(369.5, -1428.9) * mm, "end": v(1322.86, -278.9) * mm, "construction": true});
            skLineSegment(sketch, "E84", {"start": v(404.04, -1418.56) * mm, "end": v(429.57, -1387.77) * mm});
            skLineSegment(sketch, "E85", {"start": v(429.57, -1387.77) * mm, "end": v(398.77, -1362.24) * mm});
            skLineSegment(sketch, "E86", {"start": v(398.77, -1362.24) * mm, "end": v(373.24, -1393.03) * mm});
            skLineSegment(sketch, "E87", {"start": v(373.24, -1393.03) * mm, "end": v(404.04, -1418.56) * mm});
            skSolve(sketch);
        }
        {
            var Q0;
            Q0=makeQuery(id+"F25.imprint","IMPRINT",FACE,{"disambiguationData":[TD([[makeQuery(id+"F25.imprint","IMPRINT",EDGE,{"derivedFrom":sQuery(id+"F25.wireOp",EDGE,"E81")}),-1.0]])]});
            var Q1;
            Q1=makeQuery(id+"F25.imprint","IMPRINT",FACE,{"disambiguationData":[TD([[makeQuery(id+"F25.imprint","IMPRINT",EDGE,{"derivedFrom":sQuery(id+"F25.wireOp",EDGE,"E76")}),-1.0]])]});
            var Q2;
            Q2=makeQuery(id+"F25.imprint","IMPRINT",FACE,{"disambiguationData":[TD([[makeQuery(id+"F25.imprint","IMPRINT",EDGE,{"derivedFrom":sQuery(id+"F25.wireOp",EDGE,"E84")}),1.0]])]});
            extrude(context, id + "F26", {"entities" : qUnion([Q0, Q1, Q2]), "depth" : 1500 * mm, "offsetDistance" : 25 * mm});
        }
        {
            var Q0;
            Q0=makeQuery(id+"F26.opExtrude","SWEPT_FACE",FACE,{"disambiguationData":[OSD([sQuery(id+"F25.wireOp",EDGE,"E79")])]});
            var sketch = newSketch(context, id + "F27", { "sketchPlane" : qUnion([Q0])});
            skLineSegment(sketch, "E88.bottom", {"start": v(1176.4, 1525) * mm, "end": v(1216.4, 1525) * mm});
            skLineSegment(sketch, "E88.top", {"start": v(1176.4, 1485) * mm, "end": v(1216.4, 1485) * mm});
            skLineSegment(sketch, "E88.left", {"start": v(1176.4, 1525) * mm, "end": v(1176.4, 1485) * mm});
            skLineSegment(sketch, "E88.right", {"start": v(1216.4, 1525) * mm, "end": v(1216.4, 1485) * mm});
            skLineSegment(sketch, "E89.bottom", {"start": v(1176.4, 25) * mm, "end": v(1216.4, 25) * mm});
            skLineSegment(sketch, "E89.top", {"start": v(1176.4, 65) * mm, "end": v(1216.4, 65) * mm});
            skLineSegment(sketch, "E89.left", {"start": v(1176.4, 25) * mm, "end": v(1176.4, 65) * mm});
            skLineSegment(sketch, "E89.right", {"start": v(1216.4, 25) * mm, "end": v(1216.4, 65) * mm});
            skSolve(sketch);
        }
        {
            var Q0;
            Q0=makeQuery(id+"F27.imprint","IMPRINT",FACE,{"disambiguationData":[TD([[makeQuery(id+"F27.imprint","IMPRINT",EDGE,{"derivedFrom":sQuery(id+"F27.wireOp",EDGE,"E88.bottom")}),1.0]])]});
            var Q1;
            Q1=makeQuery(id+"F27.imprint","IMPRINT",FACE,{"disambiguationData":[TD([[makeQuery(id+"F27.imprint","IMPRINT",EDGE,{"derivedFrom":sQuery(id+"F27.wireOp",EDGE,"E89.bottom")}),-1.0]])]});
            extrude(context, id + "F28", {"entities" : qUnion([Q0, Q1]), "depth" : 1354 * mm, "offsetDistance" : 25 * mm});
        }
        {
            var Q0;
            Q0=makeQuery(id+"F17.boolean.opBoolean","MERGE",FACE,{"derivedFrom":[makeQuery(id+"F14.boolean.opBoolean","MERGE",FACE,{"derivedFrom":[makeQuery(id+"F6.opExtrude","SWEPT_FACE",FACE,{"disambiguationData":[OSD([sQuery(id+"F4.wireOp",EDGE,"E9.left")])]}),makeQuery(id+"F14.opExtrude","CAP_FACE",FACE,{"disambiguationData":[OSD([sQuery(id+"F13.wireOp",EDGE,"E57.bottom"),sQuery(id+"F13.wireOp",EDGE,"E57.top"),sQuery(id+"F13.wireOp",EDGE,"E57.left"),sQuery(id+"F13.wireOp",EDGE,"E57.right")])],"isStart":false}),makeQuery(id+"F14.opExtrude","CAP_FACE",FACE,{"disambiguationData":[OSD([sQuery(id+"F13.wireOp",EDGE,"E65.MirrorCS"),sQuery(id+"F13.wireOp",EDGE,"E66.MirrorCS"),sQuery(id+"F13.wireOp",EDGE,"E67.MirrorCS"),sQuery(id+"F13.wireOp",EDGE,"E68.MirrorCS")])],"isStart":false})]}),makeQuery(id+"F17.opExtrude","SWEPT_FACE",FACE,{"disambiguationData":[OSD([sQuery(id+"F16.wireOp",EDGE,"E71.left")])]})]});
            var sketch = newSketch(context, id + "F29", { "sketchPlane" : qUnion([Q0])});
            skLineSegment(sketch, "E90.bottom", {"start": v(1448.9, 1125) * mm, "end": v(1408.9, 1125) * mm});
            skLineSegment(sketch, "E90.top", {"start": v(1448.9, 1085) * mm, "end": v(1408.9, 1085) * mm});
            skLineSegment(sketch, "E90.left", {"start": v(1448.9, 1125) * mm, "end": v(1448.9, 1085) * mm});
            skLineSegment(sketch, "E90.right", {"start": v(1408.9, 1125) * mm, "end": v(1408.9, 1085) * mm});
            skLineSegment(sketch, "E91.bottom", {"start": v(1408.9, 65) * mm, "end": v(1448.9, 65) * mm});
            skLineSegment(sketch, "E91.top", {"start": v(1408.9, 25) * mm, "end": v(1448.9, 25) * mm});
            skLineSegment(sketch, "E91.left", {"start": v(1408.9, 65) * mm, "end": v(1408.9, 25) * mm});
            skLineSegment(sketch, "E91.right", {"start": v(1448.9, 65) * mm, "end": v(1448.9, 25) * mm});
            skSolve(sketch);
        }
        {
            var Q0;
            Q0=makeQuery(id+"F29.imprint","IMPRINT",FACE,{"disambiguationData":[TD([[makeQuery(id+"F29.imprint","IMPRINT",EDGE,{"derivedFrom":sQuery(id+"F29.wireOp",EDGE,"E90.bottom")}),1.0]])]});
            var Q1;
            Q1=makeQuery(id+"F29.imprint","IMPRINT",FACE,{"disambiguationData":[TD([[makeQuery(id+"F29.imprint","IMPRINT",EDGE,{"derivedFrom":sQuery(id+"F29.wireOp",EDGE,"E91.bottom")}),-1.0]])]});
            extrude(context, id + "F30", {"entities" : qUnion([Q0, Q1]), "operationType" : NewBodyOperationType.ADD, "depth" : 1120 * mm, "offsetDistance" : 25 * mm});
        }
        {
            var Q0;
            Q0=makeQuery(id+"F30.opExtrude","SWEPT_FACE",FACE,{"disambiguationData":[OSD([sQuery(id+"F29.wireOp",EDGE,"E91.bottom")])]});
            var sketch = newSketch(context, id + "F31", { "sketchPlane" : qUnion([Q0])});
            skLineSegment(sketch, "E92.bottom", {"start": v(-820.5, -1408.9) * mm, "end": v(-860.5, -1408.9) * mm});
            skLineSegment(sketch, "E92.top", {"start": v(-820.5, -1448.9) * mm, "end": v(-860.5, -1448.9) * mm});
            skLineSegment(sketch, "E92.left", {"start": v(-820.5, -1408.9) * mm, "end": v(-820.5, -1448.9) * mm});
            skLineSegment(sketch, "E92.right", {"start": v(-860.5, -1408.9) * mm, "end": v(-860.5, -1448.9) * mm});
            skSolve(sketch);
        }
        {
            var Q0;
            Q0=makeQuery(id+"F31.imprint","IMPRINT",FACE,{"disambiguationData":[TD([[makeQuery(id+"F31.imprint","IMPRINT",EDGE,{"derivedFrom":sQuery(id+"F31.wireOp",EDGE,"E92.bottom")}),1.0]])]});
            extrude(context, id + "F32", {"entities" : qUnion([Q0]), "operationType" : NewBodyOperationType.ADD, "depth" : 1060 * mm, "offsetDistance" : 25 * mm, "hasSecondDirection" : true, "secondDirectionOppositeDirection" : true, "secondDirectionDepth" : 40 * mm});
        }
        {
            var Q0;
            Q0=makeQuery(id+"F32.boolean.opBoolean","MERGE",FACE,{"derivedFrom":[makeQuery(id+"F30.opExtrude","SWEPT_FACE",FACE,{"disambiguationData":[OSD([sQuery(id+"F29.wireOp",EDGE,"E90.left")])]}),makeQuery(id+"F30.opExtrude","SWEPT_FACE",FACE,{"disambiguationData":[OSD([sQuery(id+"F29.wireOp",EDGE,"E91.right")])]}),makeQuery(id+"F32.opExtrude","SWEPT_FACE",FACE,{"disambiguationData":[OSD([sQuery(id+"F31.wireOp",EDGE,"E92.top")])]})]});
            var sketch = newSketch(context, id + "F33", { "sketchPlane" : qUnion([Q0])});
            skLineSegment(sketch, "E93.bottom", {"start": v(-860.5, 1125) * mm, "end": v(-820.5, 1125) * mm});
            skLineSegment(sketch, "E93.top", {"start": v(-860.5, 1085) * mm, "end": v(-820.5, 1085) * mm});
            skLineSegment(sketch, "E93.left", {"start": v(-860.5, 1125) * mm, "end": v(-860.5, 1085) * mm});
            skLineSegment(sketch, "E93.right", {"start": v(-820.5, 1125) * mm, "end": v(-820.5, 1085) * mm});
            skSolve(sketch);
        }
        {
            var Q0;
            Q0=makeQuery(id+"F33.imprint","IMPRINT",FACE,{"disambiguationData":[TD([[makeQuery(id+"F33.imprint","IMPRINT",EDGE,{"derivedFrom":sQuery(id+"F33.wireOp",EDGE,"E93.bottom")}),-1.0]])]});
            extrude(context, id + "F34", {"entities" : qUnion([Q0]), "operationType" : NewBodyOperationType.ADD, "depth" : 400 * mm, "offsetDistance" : 25 * mm});
        }
        {
            var Q0;
            Q0=makeQuery(id+"F4.imprint","IMPRINT",FACE,{"disambiguationData":[TD([[makeQuery(id+"F4.imprint","IMPRINT",EDGE,{"derivedFrom":sQuery(id+"F4.wireOp",EDGE,"E6.bottom")}),1.0]])]});
            cPlane(context, id + "F35", {"entities" : qUnion([Q0]), "cplaneType" : CPlaneType.OFFSET, "offset" : 300 * mm, "width" : 150 * mm, "height" : 150 * mm});
        }
        {
            var Q0;
            Q0=qCreatedBy(id+"F35.planeOp",FACE);
            var sketch = newSketch(context, id + "F36", { "sketchPlane" : qUnion([Q0])});
            skCircle(sketch, "E94", {"center": v(-1590.5, -1428.9) * mm, "radius": 20 * mm});
            skSolve(sketch);
        }
        {
            var Q0;
            Q0=makeQuery(id+"F36.imprint","IMPRINT",FACE,{"disambiguationData":[TD([[makeQuery(id+"F36.imprint","IMPRINT",EDGE,{"derivedFrom":sQuery(id+"F36.wireOp",EDGE,"E94")}),1.0]])]});
            extrude(context, id + "F37", {"entities" : qUnion([Q0]), "depth" : 40 * mm, "offsetDistance" : 25 * mm});
        }
        {
            var Q0;
            Q0=makeQuery(id+"F4.imprint","IMPRINT",FACE,{"disambiguationData":[TD([[makeQuery(id+"F4.imprint","IMPRINT",EDGE,{"derivedFrom":sQuery(id+"F4.wireOp",EDGE,"E6.bottom")}),1.0]])]});
            cPlane(context, id + "F38", {"entities" : qUnion([Q0]), "cplaneType" : CPlaneType.OFFSET, "offset" : 800 * mm, "width" : 150 * mm, "height" : 150 * mm});
        }
        {
            var Q0;
            Q0=qCreatedBy(id+"F38.planeOp",FACE);
            var sketch = newSketch(context, id + "F39", { "sketchPlane" : qUnion([Q0])});
            skCircle(sketch, "E95", {"center": v(-1590.5, -1428.9) * mm, "radius": 20 * mm});
            skSolve(sketch);
        }
        {
            var Q0;
            Q0=makeQuery(id+"F39.imprint","IMPRINT",FACE,{"disambiguationData":[TD([[makeQuery(id+"F39.imprint","IMPRINT",EDGE,{"derivedFrom":sQuery(id+"F39.wireOp",EDGE,"E95")}),1.0]])]});
            extrude(context, id + "F40", {"entities" : qUnion([Q0]), "depth" : 40 * mm, "offsetDistance" : 25 * mm});
        }
        {
            var Q0;
            Q0=makeQuery(id+"F4.imprint","IMPRINT",FACE,{"disambiguationData":[TD([[makeQuery(id+"F4.imprint","IMPRINT",EDGE,{"derivedFrom":sQuery(id+"F4.wireOp",EDGE,"E6.bottom")}),1.0]])]});
            cPlane(context, id + "F41", {"entities" : qUnion([Q0]), "cplaneType" : CPlaneType.OFFSET, "offset" : 100 * mm, "width" : 150 * mm, "height" : 150 * mm});
        }
        {
            var Q0;
            Q0=qCreatedBy(id+"F41.planeOp",FACE);
            var sketch = newSketch(context, id + "F42", { "sketchPlane" : qUnion([Q0])});
            skLineSegment(sketch, "E96.bottom", {"start": v(-1560.5, -1407.16) * mm, "end": v(-1520.5, -1407.16) * mm});
            skLineSegment(sketch, "E96.top", {"start": v(-1560.5, -1447.16) * mm, "end": v(-1520.5, -1447.16) * mm});
            skLineSegment(sketch, "E96.left", {"start": v(-1560.5, -1407.16) * mm, "end": v(-1560.5, -1447.16) * mm});
            skLineSegment(sketch, "E96.right", {"start": v(-1520.5, -1407.16) * mm, "end": v(-1520.5, -1447.16) * mm});
            skLineSegment(sketch, "E97.bottom", {"start": v(-870.5, -1408.9) * mm, "end": v(-910.5, -1408.9) * mm});
            skLineSegment(sketch, "E97.top", {"start": v(-870.5, -1448.9) * mm, "end": v(-910.5, -1448.9) * mm});
            skLineSegment(sketch, "E97.left", {"start": v(-870.5, -1408.9) * mm, "end": v(-870.5, -1448.9) * mm});
            skLineSegment(sketch, "E97.right", {"start": v(-910.5, -1408.9) * mm, "end": v(-910.5, -1448.9) * mm});
            skSolve(sketch);
        }
        {
            var Q0;
            Q0=makeQuery(id+"F42.imprint","IMPRINT",FACE,{"disambiguationData":[TD([[makeQuery(id+"F42.imprint","IMPRINT",EDGE,{"derivedFrom":sQuery(id+"F42.wireOp",EDGE,"E96.bottom")}),-1.0]])]});
            var Q1;
            Q1=makeQuery(id+"F42.imprint","IMPRINT",FACE,{"disambiguationData":[TD([[makeQuery(id+"F42.imprint","IMPRINT",EDGE,{"derivedFrom":sQuery(id+"F42.wireOp",EDGE,"E97.bottom")}),1.0]])]});
            extrude(context, id + "F43", {"entities" : qUnion([Q0, Q1]), "depth" : 1000 * mm, "offsetDistance" : 25 * mm});
        }
        {
            var Q0;
            Q0=makeQuery(id+"F43.opExtrude","SWEPT_FACE",FACE,{"disambiguationData":[OSD([sQuery(id+"F42.wireOp",EDGE,"E97.right")])]});
            var sketch = newSketch(context, id + "F44", { "sketchPlane" : qUnion([Q0])});
            skLineSegment(sketch, "E98.bottom", {"start": v(1408.9, 1125) * mm, "end": v(1448.9, 1125) * mm});
            skLineSegment(sketch, "E98.top", {"start": v(1408.9, 1085) * mm, "end": v(1448.9, 1085) * mm});
            skLineSegment(sketch, "E98.left", {"start": v(1408.9, 1125) * mm, "end": v(1408.9, 1085) * mm});
            skLineSegment(sketch, "E98.right", {"start": v(1448.9, 1125) * mm, "end": v(1448.9, 1085) * mm});
            skLineSegment(sketch, "E99.bottom", {"start": v(1408.9, 125) * mm, "end": v(1448.9, 125) * mm});
            skLineSegment(sketch, "E99.top", {"start": v(1408.9, 165) * mm, "end": v(1448.9, 165) * mm});
            skLineSegment(sketch, "E99.left", {"start": v(1408.9, 125) * mm, "end": v(1408.9, 165) * mm});
            skLineSegment(sketch, "E99.right", {"start": v(1448.9, 125) * mm, "end": v(1448.9, 165) * mm});
            skSolve(sketch);
        }
        {
            var Q0;
            Q0=makeQuery(id+"F44.imprint","IMPRINT",FACE,{"disambiguationData":[TD([[makeQuery(id+"F44.imprint","IMPRINT",EDGE,{"derivedFrom":sQuery(id+"F44.wireOp",EDGE,"E98.bottom")}),-1.0]])]});
            var Q1;
            Q1=makeQuery(id+"F44.imprint","IMPRINT",FACE,{"disambiguationData":[TD([[makeQuery(id+"F44.imprint","IMPRINT",EDGE,{"derivedFrom":sQuery(id+"F44.wireOp",EDGE,"E99.bottom")}),1.0]])]});
            extrude(context, id + "F45", {"entities" : qUnion([Q0, Q1]), "depth" : 610 * mm, "offsetDistance" : 25 * mm});
        }
        {
            var Q0;
            Q0=makeQuery(id+"F8.opExtrude","SWEPT_FACE",FACE,{"disambiguationData":[OSD([sQuery(id+"F7.wireOp",EDGE,"E10.right")])]});
            var sketch = newSketch(context, id + "F46", { "sketchPlane" : qUnion([Q0])});
            skLineSegment(sketch, "E100.bottom", {"start": v(-249.55, 1525) * mm, "end": v(1550.45, 1525) * mm});
            skLineSegment(sketch, "E100.top", {"start": v(-249.55, 25) * mm, "end": v(1500.45, 25) * mm});
            skLineSegment(sketch, "E100.left", {"start": v(-249.55, 1525) * mm, "end": v(-249.55, 25) * mm});
            skLineSegment(sketch, "E100.right", {"start": v(1550.45, 1525) * mm, "end": v(1550.45, 455) * mm});
            skLineSegment(sketch, "E101", {"start": v(1550.45, 455) * mm, "end": v(1500.45, 455) * mm});
            skLineSegment(sketch, "E102", {"start": v(1500.45, 455) * mm, "end": v(1500.45, 25) * mm});
            skSolve(sketch);
        }
        {
            var Q0;
            Q0 = qSketchRegion(id + "F46", true);
            extrude(context, id + "F47", {"entities" : qUnion([Q0]), "depth" : 10 * mm, "offsetDistance" : 25 * mm});
        }
        {
            var Q0;
            Q0=makeQuery(id+"F26.opExtrude","SWEPT_FACE",FACE,{"disambiguationData":[OSD([sQuery(id+"F25.wireOp",EDGE,"E84")])]});
            var sketch = newSketch(context, id + "F48", { "sketchPlane" : qUnion([Q0])});
            skLineSegment(sketch, "E103.bottom", {"start": v(-834.22, 1525) * mm, "end": v(599.81, 1525) * mm});
            skLineSegment(sketch, "E103.top", {"start": v(-834.22, 25) * mm, "end": v(-220.19, 25) * mm});
            skLineSegment(sketch, "E103.left", {"start": v(-834.22, 1525) * mm, "end": v(-834.22, 25) * mm});
            skLineSegment(sketch, "E103.right", {"start": v(599.81, 1525) * mm, "end": v(599.81, 1075) * mm});
            skLineSegment(sketch, "E104.top", {"start": v(599.81, 1075) * mm, "end": v(-220.19, 1075) * mm});
            skLineSegment(sketch, "E104.right", {"start": v(-220.19, 25) * mm, "end": v(-220.19, 1075) * mm});
            skSolve(sketch);
        }
        {
            var Q0;
            Q0 = qSketchRegion(id + "F48", true);
            extrude(context, id + "F49", {"entities" : qUnion([Q0]), "depth" : 10 * mm, "offsetDistance" : 25 * mm});
        }
        {
            var Q0;
            {var subQ1=makeQuery(id+"F30.opExtrude","SWEPT_FACE",FACE,{"disambiguationData":[OSD([sQuery(id+"F29.wireOp",EDGE,"E90.left")])]});var subQ2=sQuery(id+"F31.wireOp",EDGE,"E92.top");var subQ3=makeQuery(id+"F32.opExtrude","SWEPT_FACE",FACE,{"disambiguationData":[OSD([subQ2])]});var subQ4=makeQuery(id+"F30.opExtrude","SWEPT_FACE",FACE,{"disambiguationData":[OSD([sQuery(id+"F29.wireOp",EDGE,"E91.right")])]});Q0=makeQuery(id+"F34.boolean.opBoolean","SPLIT",FACE,{"disambiguationData":[TD([makeQuery(id+"F17.opExtrude","SWEPT_FACE",FACE,{"disambiguationData":[OSD([sQuery(id+"F16.wireOp",EDGE,"E71.bottom")])]})])],"derivedFrom":makeQuery(id+"F32.boolean.opBoolean","MERGE",FACE,{"derivedFrom":[subQ1,subQ4,subQ3]})});}
            var sketch = newSketch(context, id + "F50", { "sketchPlane" : qUnion([Q0])});
            skLineSegment(sketch, "E105.bottom", {"start": v(-820.5, 1125) * mm, "end": v(299.84, 1125) * mm});
            skLineSegment(sketch, "E105.top", {"start": v(-820.5, 24.48) * mm, "end": v(287.7, 24.48) * mm});
            skLineSegment(sketch, "E105.left", {"start": v(-820.5, 1125) * mm, "end": v(-820.5, 1085) * mm});
            skLineSegment(sketch, "E105.right", {"start": v(299.84, 1125) * mm, "end": v(299.84, 1085) * mm});
            skLineSegment(sketch, "E106.bottom", {"start": v(-820.5, 1085) * mm, "end": v(-860.07, 1085) * mm});
            skLineSegment(sketch, "E106.right", {"start": v(-860.07, 1085) * mm, "end": v(-860.07, 65.11) * mm});
            skLineSegment(sketch, "E107.bottom", {"start": v(299.5, 1085) * mm, "end": v(337.7, 1085) * mm});
            skLineSegment(sketch, "E107.top", {"start": v(299.5, 65.11) * mm, "end": v(299.84, 65.11) * mm});
            skLineSegment(sketch, "E107.right", {"start": v(337.7, 1085) * mm, "end": v(337.7, 454.48) * mm});
            skLineSegment(sketch, "E108.trimOffspring", {"start": v(299.84, 65.11) * mm, "end": v(299.84, 24.48) * mm});
            skPoint(sketch, "E109.trimOffspring.start.orphan", {"position": v(-820.5, 65.11) * mm});
            skLineSegment(sketch, "E110.top", {"start": v(-860.07, 24.48) * mm, "end": v(-820.5, 24.48) * mm});
            skLineSegment(sketch, "E110.left", {"start": v(-860.07, 65.11) * mm, "end": v(-860.07, 24.48) * mm});
            skLineSegment(sketch, "E111.bottom", {"start": v(337.7, 454.48) * mm, "end": v(287.7, 454.48) * mm});
            skLineSegment(sketch, "E111.top", {"start": v(299.84, 24.48) * mm, "end": v(287.7, 24.48) * mm});
            skLineSegment(sketch, "E111.left", {"start": v(337.7, 65.11) * mm, "end": v(337.7, 24.48) * mm});
            skLineSegment(sketch, "E111.right", {"start": v(287.7, 454.48) * mm, "end": v(287.7, 24.48) * mm});
            skPoint(sketch, "E112.orphan", {"position": v(337.7, 65.11) * mm});
            skSolve(sketch);
        }
        {
            var Q0;
            Q0 = qSketchRegion(id + "F50", true);
            extrude(context, id + "F51", {"entities" : qUnion([Q0]), "depth" : 10 * mm, "offsetDistance" : 25 * mm});
        }
        {
            var Q0;
            Q0=makeQuery(id+"F43.opExtrude","SWEPT_FACE",FACE,{"disambiguationData":[OSD([sQuery(id+"F42.wireOp",EDGE,"E96.top")])]});
            var sketch = newSketch(context, id + "F52", { "sketchPlane" : qUnion([Q0])});
            skLineSegment(sketch, "E113.bottom", {"start": v(-1560.5, 1125) * mm, "end": v(-870.5, 1125) * mm});
            skLineSegment(sketch, "E113.top", {"start": v(-1560.5, 125) * mm, "end": v(-870.5, 125) * mm});
            skLineSegment(sketch, "E113.left", {"start": v(-1560.5, 1125) * mm, "end": v(-1560.5, 125) * mm});
            skLineSegment(sketch, "E113.right", {"start": v(-870.5, 1125) * mm, "end": v(-870.5, 125) * mm});
            skSolve(sketch);
        }
        {
            var Q0;
            Q0 = qSketchRegion(id + "F52", true);
            extrude(context, id + "F53", {"entities" : qUnion([Q0]), "depth" : 10 * mm, "offsetDistance" : 25 * mm});
        }
        {
            var Q0;
            Q0=makeQuery(id+"F34.boolean.opBoolean","MERGE",FACE,{"derivedFrom":[makeQuery(id+"F32.boolean.opBoolean","MERGE",FACE,{"derivedFrom":[makeQuery(id+"F30.opExtrude","SWEPT_FACE",FACE,{"disambiguationData":[OSD([sQuery(id+"F29.wireOp",EDGE,"E90.bottom")])]}),makeQuery(id+"F32.opExtrude","CAP_FACE",FACE,{"disambiguationData":[OSD([sQuery(id+"F31.wireOp",EDGE,"E92.bottom"),sQuery(id+"F31.wireOp",EDGE,"E92.top"),sQuery(id+"F31.wireOp",EDGE,"E92.left"),sQuery(id+"F31.wireOp",EDGE,"E92.right")])],"isStart":false})]}),makeQuery(id+"F34.opExtrude","SWEPT_FACE",FACE,{"disambiguationData":[OSD([sQuery(id+"F33.wireOp",EDGE,"E93.bottom")])]})]});
            var sketch = newSketch(context, id + "F54", { "sketchPlane" : qUnion([Q0])});
            skLineSegment(sketch, "E114.bottom", {"start": v(-860.5, -1408.9) * mm, "end": v(299.5, -1408.9) * mm});
            skLineSegment(sketch, "E114.top", {"start": v(-860.5, -1848.9) * mm, "end": v(339.47, -1848.9) * mm});
            skLineSegment(sketch, "E114.left", {"start": v(-860.5, -1408.9) * mm, "end": v(-860.5, -1848.9) * mm});
            skLineSegment(sketch, "E114.right", {"start": v(339.47, -1448.9) * mm, "end": v(339.47, -1848.9) * mm});
            skLineSegment(sketch, "E115.top", {"start": v(339.47, -1448.9) * mm, "end": v(299.5, -1448.9) * mm});
            skLineSegment(sketch, "E115.right", {"start": v(299.5, -1408.9) * mm, "end": v(299.5, -1448.9) * mm});
            skSolve(sketch);
        }
        {
            var Q0;
            Q0 = qSketchRegion(id + "F54", true);
            extrude(context, id + "F55", {"entities" : qUnion([Q0]), "depth" : 10 * mm, "offsetDistance" : 25 * mm});
        }
    });
